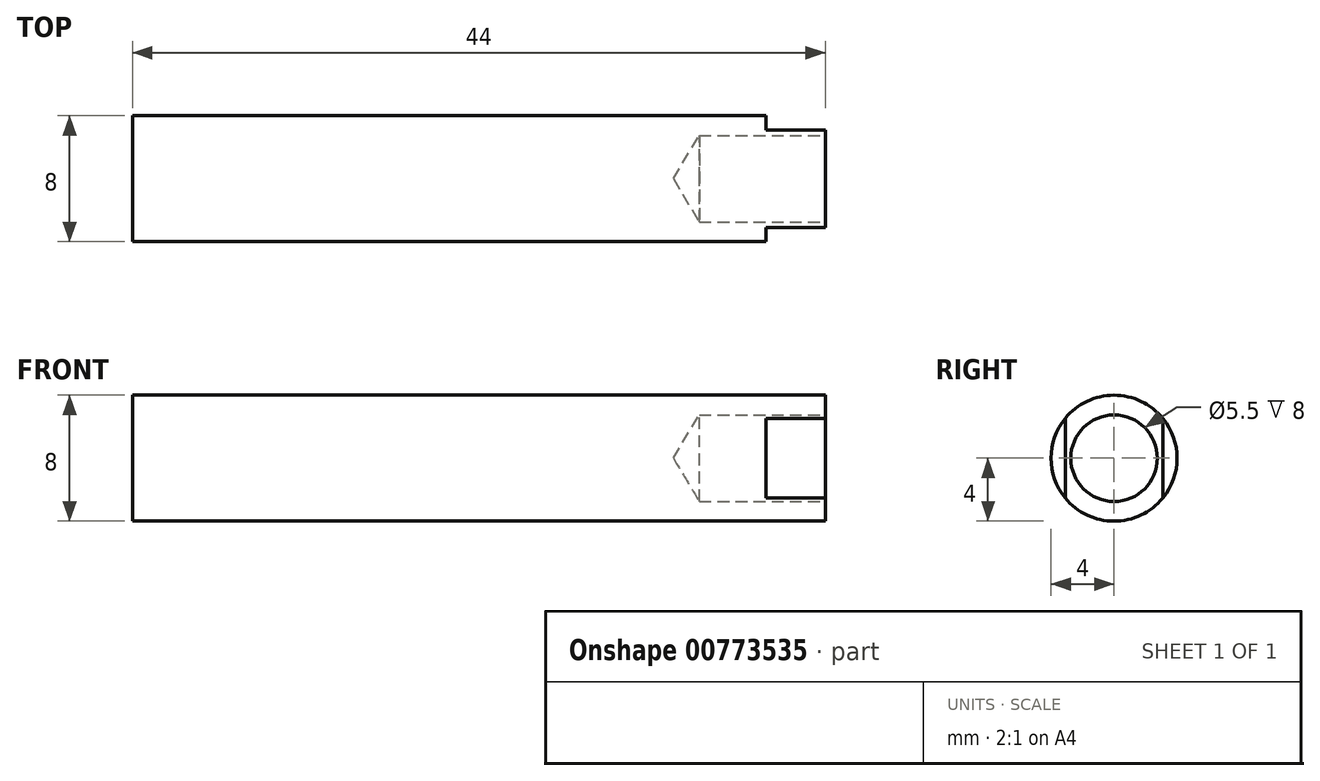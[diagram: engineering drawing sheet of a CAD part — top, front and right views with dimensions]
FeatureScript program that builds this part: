
annotation { "Feature Type Name" : "Feature", "Feature Type Description" : "" }
export const myFeature = defineFeature(function(context is Context, id is Id, definition is map)
    precondition{}
    {
        {
            var Q0;
            Q0=qCreatedBy(makeId("Right.planeOp"),FACE);
            var sketch = newSketch(context, id + "F0", { "sketchPlane" : qUnion([Q0])});
            skCircle(sketch, "E0", {"center": v(0, 0) * mm, "radius": 4 * mm});
            skSolve(sketch);
        }
        {
            var Q0;
            Q0 = qSketchRegion(id + "F0", true);
            extrude(context, id + "F1", {"entities" : qUnion([Q0]), "endBound" : BoundingType.SYMMETRIC, "depth" : 44 * mm, "offsetDistance" : 25 * mm});
        }
        {
            var Q0;
            Q0=qCreatedBy(makeId("Top.planeOp"),FACE);
            var sketch = newSketch(context, id + "F2", { "sketchPlane" : qUnion([Q0])});
            skLineSegment(sketch, "E1", {"start": v(22, -3.1) * mm, "end": v(18.23, -3.1) * mm});
            skLineSegment(sketch, "E2", {"start": v(18.23, -3.1) * mm, "end": v(18.23, -4.5) * mm});
            skLineSegment(sketch, "E3", {"start": v(18.23, -4.5) * mm, "end": v(22, -4.5) * mm});
            skLineSegment(sketch, "E4", {"start": v(22, -4.5) * mm, "end": v(22, -3.1) * mm});
            skLineSegment(sketch, "E5", {"start": v(0, 0) * mm, "end": v(25.3, 0) * mm, "construction": true});
            skLineSegment(sketch, "E6.MirrorCS", {"start": v(22, 3.1) * mm, "end": v(18.23, 3.1) * mm});
            skLineSegment(sketch, "E7.MirrorCS", {"start": v(18.23, 3.1) * mm, "end": v(18.23, 4.5) * mm});
            skLineSegment(sketch, "E8.MirrorCS", {"start": v(18.23, 4.5) * mm, "end": v(22, 4.5) * mm});
            skLineSegment(sketch, "E9.MirrorCS", {"start": v(22, 4.5) * mm, "end": v(22, 3.1) * mm});
            skSolve(sketch);
        }
        {
            var Q0;
            Q0=makeQuery(id+"F1.opExtrude","CAP_FACE",FACE,{"disambiguationData":[OSD([sQuery(id+"F0.wireOp",EDGE,"E0")])],"isStart":false});
            var sketch = newSketch(context, id + "F3", { "sketchPlane" : qUnion([Q0])});
            skCircle(sketch, "E10", {"center": v(0, 0) * mm, "radius": 2.5 * mm});
            skSolve(sketch);
        }
        {
            var Q0;
            Q0=sQuery(id+"F3.wireOp",VERTEX,"E10.center");
            var Q1;
            Q1=makeQuery(id+"F1.opExtrude","SWEPT_BODY",BODY,{"disambiguationData":[OSD([sQuery(id+"F0.wireOp",EDGE,"E0")])]});
            hole(context, id + "F4", {"style" : HoleStyle.SIMPLE, "endStyle" : HoleEndStyle.BLIND, "standardTappedOrClearance" : lookupTablePath({ "standard" : "ISO", "fit" : "Normal", "size" : "M5", "type" : "Clearance" }), "standardBlindInLast" : lookupTablePath({ "fit" : "Standard", "standard" : "ISO", "size" : "M5", "type" : "Clearance" }), "holeDiameter" : 5.5 * mm, "majorDiameter" : 5 * mm, "holeDepth" : 8 * mm, "isTappedThrough" : true, "tappedDepth" : 12 * mm, "tapClearance" : 3, "locations" : qUnion([Q0]), "scope" : qUnion([Q1])});
        }
        {
            var Q0;
            Q0=makeQuery(id+"F2.imprint","IMPRINT",FACE,{"disambiguationData":[TD([[makeQuery(id+"F2.imprint","IMPRINT",EDGE,{"derivedFrom":sQuery(id+"F2.wireOp",EDGE,"E6.MirrorCS")}),-1.0]])]});
            var Q1;
            Q1=makeQuery(id+"F2.imprint","IMPRINT",FACE,{"disambiguationData":[TD([[makeQuery(id+"F2.imprint","IMPRINT",EDGE,{"derivedFrom":sQuery(id+"F2.wireOp",EDGE,"E1")}),1.0]])]});
            extrude(context, id + "F5", {"entities" : qUnion([Q0, Q1]), "operationType" : NewBodyOperationType.REMOVE, "endBound" : BoundingType.SYMMETRIC, "depth" : 25 * mm, "offsetDistance" : 25 * mm});
        }
    });
